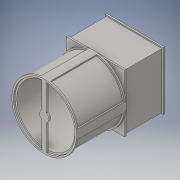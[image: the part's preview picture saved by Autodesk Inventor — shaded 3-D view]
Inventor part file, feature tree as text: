
AUTODESK INVENTOR PART (.ipt)
format: ipt  version: 2016 (Build 200138000, 138)  size: 232,448 bytes
history: native  units: in
note: dims shown in document units (in); Inventor stores cm internally (conversion verified against a paired STEP export)
features: extrude x7, sketch x7
ambient origin geometry x8: Origin, YZ Plane, XZ Plane, XY Plane, X Axis, Y Axis, Z Axis, Center Point
bodies: Solid1 (feature_tree)
feature tree (14):
  extrude  "Extrusion1"  Depth=6.25in
  extrude  "Extrusion2"  Depth=6.0in
  extrude  "Extrusion3"  Depth=5.64in
  extrude  "Extrusion4"  Depth=4.0in TaperAngle=0.0deg
  extrude  "Extrusion5"  Depth=0.18in
  extrude  "Extrusion6"  Depth=0.18in
  extrude  "Extrusion7"  Depth=0.18in
  sketch  "Sketch1"  dims[d0=6.25in d1=6.25in]
  sketch  "Sketch2"  dims[d2=0.18in d3=0.0in d4=6.0in]
  sketch  "Sketch3"  dims[d5=6.0in d6=5.64in]
  sketch  "Sketch4"  dims[d7=5.64in d8=4.0in d9=0.0in]
  sketch  "Sketch5"  dims[d10=0.18in d11=0.0in d12=1.0in]
  sketch  "Sketch6"  dims[d13=0.18in d14=0.0in d15=7.0in]
  sketch  "Sketch7"  dims[d16=0.18in d17=0.0in d22=0.18in d23=0.18in d24=0.18in d25=0.18in d26=0.18in d27=0.18in d28=0.18in d29=0.5621in d30=0.18in d31=0.6747in d32=0.18in d33=0.18in d34=0.18in d35=0.18in d36=6.28in d37=5.0in d38=0.0in d39=1.0in d40=0.5in d41=0.18in d42=0.0in]
